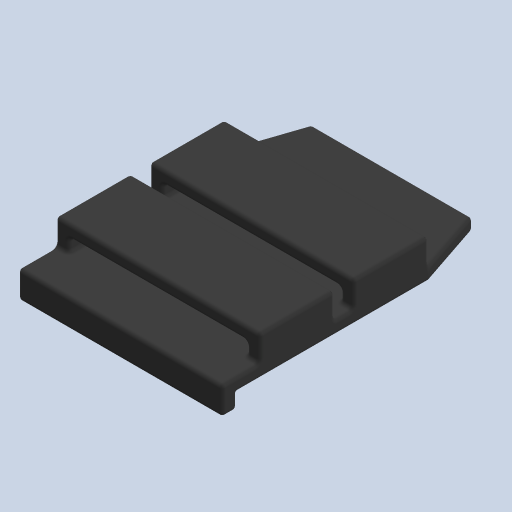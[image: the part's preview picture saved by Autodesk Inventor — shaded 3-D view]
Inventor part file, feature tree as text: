
AUTODESK INVENTOR PART (.ipt)
format: ipt  version: 2023 (Build 270158000, 158)  size: 558,080 bytes
history: native  units: mm
features: other x10, extrude x6, fillet x2, pattern_linear x1, plane x1
ambient origin geometry x8: Origin, YZ Plane, XZ Plane, XY Plane, X Axis, Y Axis, Z Axis, Center Point
bodies: Solid1 (feature_tree)
feature tree (20):
  other  "NP2-Alpha_Payload.ipt"
  other  "Sk:Params"
  other  "Sk:Base"
  extrude  "Ex:Base"  Depth=10.0mm
  extrude  "Ex:EndLip"  Depth=0.7mm TaperAngle=0.0deg
  other  "EndPlane"
  other  "Sk:Slot"
  extrude  "Ex:Slot1"  Depth=0.8mm TaperAngle=0.0deg
  extrude  "Ex:SlotEnd"  Depth=0.7mm
  extrude  "Ex:TaperSection"  Depth=0.7mm
  pattern_linear  "Pat:Slot2"  Spacing1=0.7mm  [1 undecoded]
  plane  "Work Plane5"
  extrude  "Ex:InsideStorage"  Depth=0.7mm
  fillet  "Fillet:ExcludeLine"  Radius=0.2mm
  fillet  "Fillet:Final"  Radius=4.0mm
  other  "TaggingFeature1"
  other  "Sk:EndLip"
  other  "Sk:InsideStorage"
  other  "Solid1::NP2-Alpha_Payload.ipt"
  other  "Srf1"
note: 1 required parameter value undecoded (feature->parameter linkage not recoverable at this tier; creation-order binding heuristic only, values carry confidence <= 0.55)
